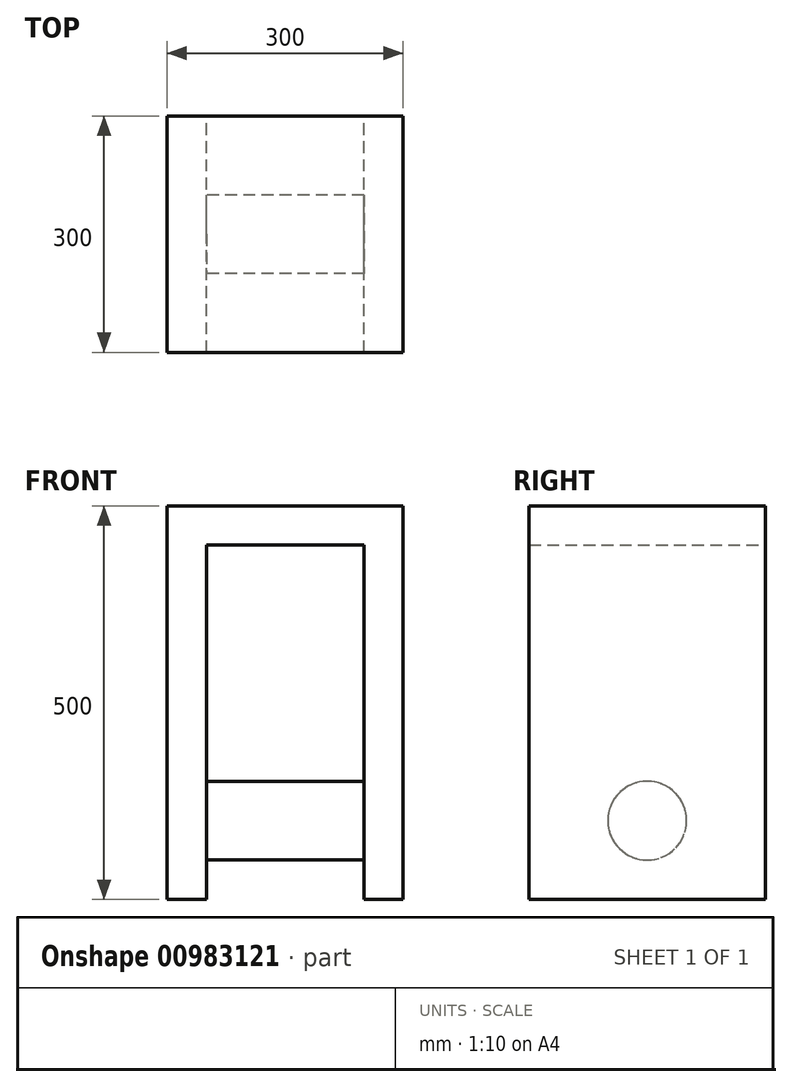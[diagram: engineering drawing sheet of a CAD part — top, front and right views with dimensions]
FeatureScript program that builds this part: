
annotation { "Feature Type Name" : "Feature", "Feature Type Description" : "" }
export const myFeature = defineFeature(function(context is Context, id is Id, definition is map)
    precondition{}
    {
        {
            var Q0;
            Q0=qCreatedBy(makeId("Front.planeOp"),FACE);
            var sketch = newSketch(context, id + "F0", { "sketchPlane" : qUnion([Q0])});
            skLineSegment(sketch, "E0", {"start": v(0, 0) * mm, "end": v(0, 500) * mm});
            skLineSegment(sketch, "E1", {"start": v(0, 500) * mm, "end": v(300, 500) * mm});
            skLineSegment(sketch, "E2", {"start": v(300, 500) * mm, "end": v(300, 0) * mm});
            skLineSegment(sketch, "E3", {"start": v(300, 0) * mm, "end": v(250, 0) * mm});
            skLineSegment(sketch, "E4", {"start": v(250, 0) * mm, "end": v(250, 450) * mm});
            skLineSegment(sketch, "E5", {"start": v(250, 450) * mm, "end": v(50, 450) * mm});
            skLineSegment(sketch, "E6", {"start": v(50, 450) * mm, "end": v(50, 0) * mm});
            skLineSegment(sketch, "E7", {"start": v(50, 0) * mm, "end": v(0, 0) * mm});
            skSolve(sketch);
        }
        {
            var Q0;
            Q0 = qSketchRegion(id + "F0", true);
            extrude(context, id + "F1", {"entities" : qUnion([Q0]), "depth" : 300 * mm, "offsetDistance" : 25 * mm});
        }
        {
            var Q0;
            Q0=qCreatedBy(makeId("Right.planeOp"),FACE);
            var sketch = newSketch(context, id + "F2", { "sketchPlane" : qUnion([Q0])});
            skCircle(sketch, "E8", {"center": v(-150, 100) * mm, "radius": 50 * mm});
            skSolve(sketch);
        }
        {
            var Q0;
            Q0 = qSketchRegion(id + "F2", true);
            var Q1;
            Q1=makeQuery(id+"F1.opExtrude","SWEPT_FACE",FACE,{"disambiguationData":[OSD([sQuery(id+"F0.wireOp",EDGE,"E4")])]});
            var Q2;
            Q2=makeQuery(id+"F1.opExtrude","SWEPT_FACE",FACE,{"disambiguationData":[OSD([sQuery(id+"F0.wireOp",EDGE,"E2")])]});
            extrude(context, id + "F3", {"entities" : qUnion([Q0, Q1]), "operationType" : NewBodyOperationType.ADD, "endBound" : BoundingType.UP_TO_SURFACE, "depth" : 450 * mm, "endBoundEntityFace" : qUnion([Q2]), "offsetDistance" : 25 * mm});
        }
    });
